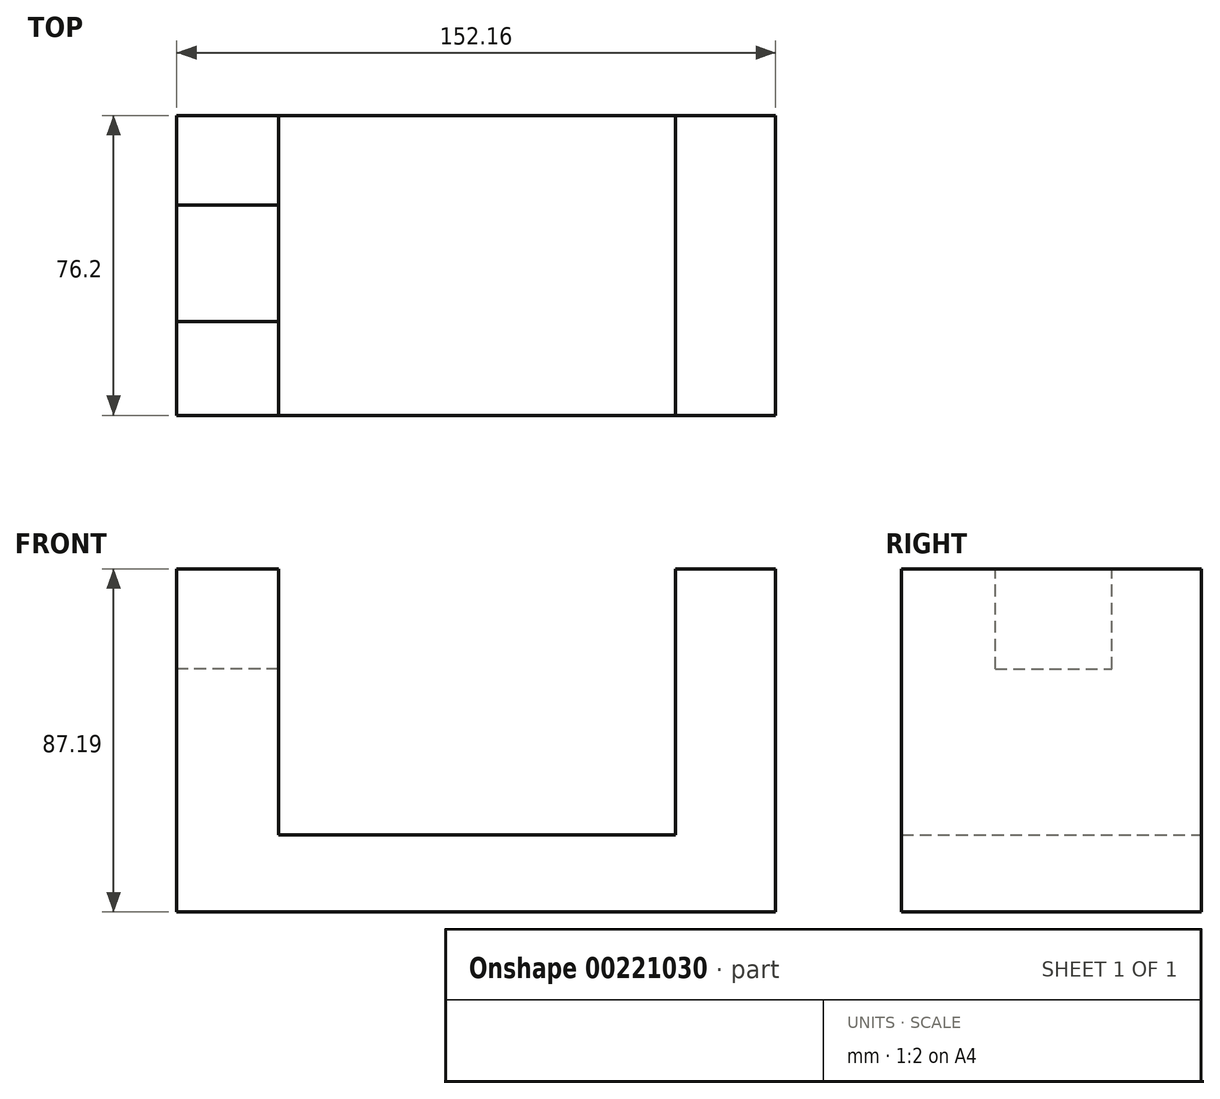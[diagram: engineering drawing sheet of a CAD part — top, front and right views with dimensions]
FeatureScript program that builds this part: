
annotation { "Feature Type Name" : "Feature", "Feature Type Description" : "" }
export const myFeature = defineFeature(function(context is Context, id is Id, definition is map)
    precondition{}
    {
        {
            var Q0;
            Q0=qCreatedBy(makeId("Front.planeOp"),FACE);
            var sketch = newSketch(context, id + "F0", { "sketchPlane" : qUnion([Q0])});
            skLineSegment(sketch, "E0.bottom", {"start": v(-76.08, 40.53) * mm, "end": v(-50.2, 40.53) * mm});
            skLineSegment(sketch, "E0.top", {"start": v(-76.08, -46.66) * mm, "end": v(76.08, -46.66) * mm});
            skLineSegment(sketch, "E0.left", {"start": v(-76.08, 40.53) * mm, "end": v(-76.08, -46.66) * mm});
            skLineSegment(sketch, "E0.right", {"start": v(76.08, 40.53) * mm, "end": v(76.08, -46.66) * mm});
            skLineSegment(sketch, "E1.top", {"start": v(-50.2, -27.12) * mm, "end": v(50.6, -27.12) * mm});
            skLineSegment(sketch, "E1.left", {"start": v(-50.2, 40.53) * mm, "end": v(-50.2, -27.12) * mm});
            skLineSegment(sketch, "E1.right", {"start": v(50.6, 40.53) * mm, "end": v(50.6, -27.12) * mm});
            skLineSegment(sketch, "E2.trimOffspring", {"start": v(50.6, 40.53) * mm, "end": v(76.08, 40.53) * mm});
            skSolve(sketch);
        }
        {
            var Q0;
            Q0=makeQuery(id+"F0.imprint","IMPRINT",FACE,{"disambiguationData":[TD([[makeQuery(id+"F0.imprint","IMPRINT",EDGE,{"derivedFrom":sQuery(id+"F0.wireOp",EDGE,"E0.bottom")}),-1.0]])]});
            extrude(context, id + "F1", {"entities" : qUnion([Q0]), "depth" : 76.2 * mm});
        }
        {
            var Q0;
            Q0=makeQuery(id+"F1.opExtrude","SWEPT_FACE",FACE,{"disambiguationData":[OSD([sQuery(id+"F0.wireOp",EDGE,"E0.bottom")])]});
            var sketch = newSketch(context, id + "F2", { "sketchPlane" : qUnion([Q0])});
            skLineSegment(sketch, "E3.bottom", {"start": v(-50.2, -22.74) * mm, "end": v(-76.08, -22.74) * mm});
            skLineSegment(sketch, "E3.top", {"start": v(-50.2, -52.4) * mm, "end": v(-76.08, -52.4) * mm});
            skLineSegment(sketch, "E3.left", {"start": v(-50.2, -22.74) * mm, "end": v(-50.2, -52.4) * mm});
            skLineSegment(sketch, "E3.right", {"start": v(-76.08, -22.74) * mm, "end": v(-76.08, -52.4) * mm});
            skSolve(sketch);
        }
        {
            var Q0;
            Q0 = qSketchRegion(id + "F2", true);
            extrude(context, id + "F3", {"entities" : qUnion([Q0]), "operationType" : NewBodyOperationType.REMOVE, "oppositeDirection" : true, "depth" : 25.4 * mm});
        }
    });
